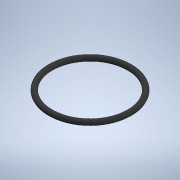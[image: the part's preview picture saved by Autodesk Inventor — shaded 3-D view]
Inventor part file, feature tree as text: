
AUTODESK INVENTOR PART (.ipt)
format: ipt  version: 2020.3 (Build 243373000, 373)  size: 121,344 bytes
history: native  units: mm
features: revolve x1, sketch x1
ambient origin geometry x8: Origin, YZ Plane, XZ Plane, XY Plane, X Axis, Y Axis, Z Axis, Center Point
bodies: Solid1 (feature_tree)
feature tree (2):
  revolve  "Revolution1"  [1 undecoded]
  sketch  "Sketch1"  dims[d0=1.78mm d1=13.45mm d2=90.0deg]
note: 1 required parameter value undecoded (feature->parameter linkage not recoverable at this tier; creation-order binding heuristic only, values carry confidence <= 0.55)
